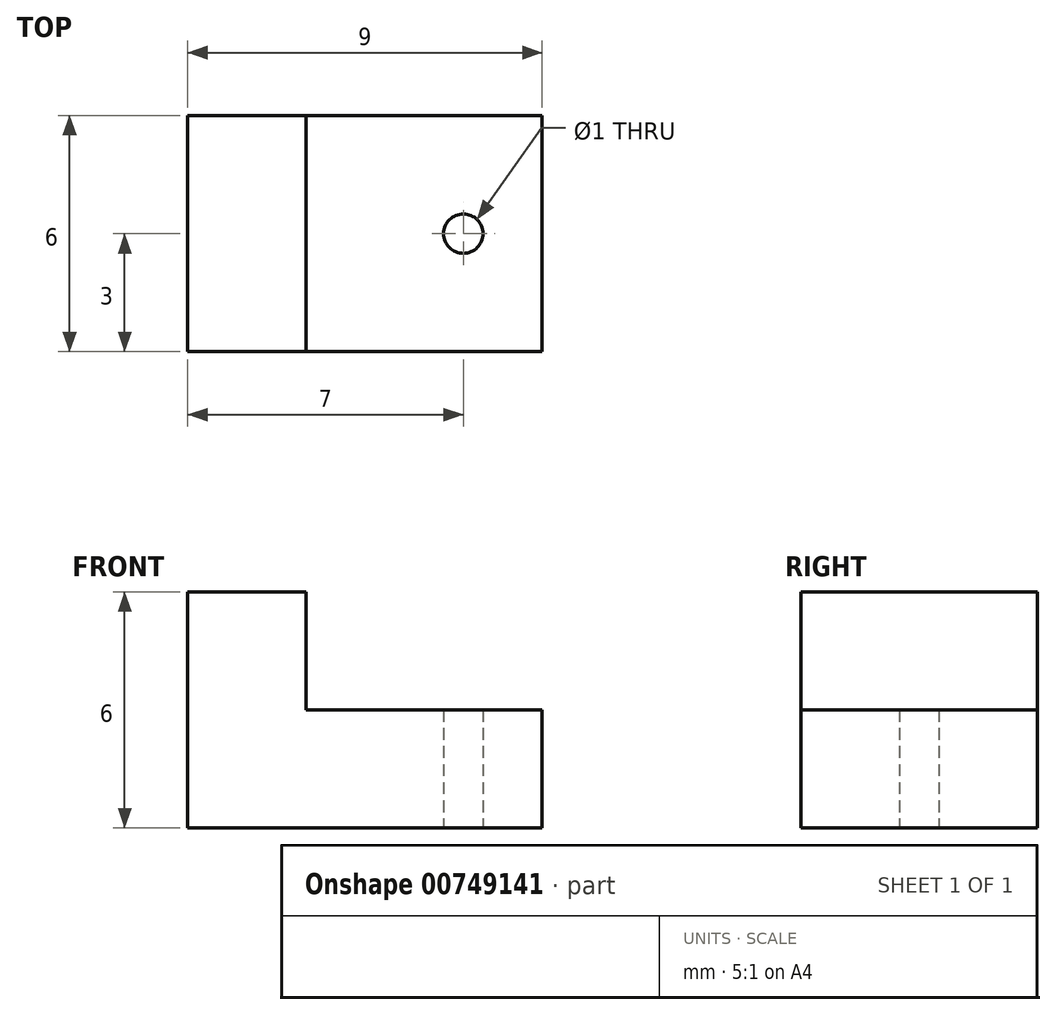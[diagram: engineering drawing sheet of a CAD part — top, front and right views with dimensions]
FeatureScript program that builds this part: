
annotation { "Feature Type Name" : "Feature", "Feature Type Description" : "" }
export const myFeature = defineFeature(function(context is Context, id is Id, definition is map)
    precondition{}
    {
        {
            var Q0;
            Q0=qCreatedBy(makeId("Top.planeOp"),FACE);
            var sketch = newSketch(context, id + "F0", { "sketchPlane" : qUnion([Q0])});
            skLineSegment(sketch, "E0.bottom", {"start": v(2, 3) * mm, "end": v(-4, 3) * mm});
            skLineSegment(sketch, "E0.top", {"start": v(2, -3) * mm, "end": v(-4, -3) * mm});
            skLineSegment(sketch, "E0.left", {"start": v(2, 3) * mm, "end": v(2, -3) * mm});
            skLineSegment(sketch, "E0.right", {"start": v(-4, 3) * mm, "end": v(-4, -3) * mm});
            skPoint(sketch, "E0.middle", {"position": v(0, 0) * mm});
            skLineSegment(sketch, "E1.bottom", {"start": v(-4, 3) * mm, "end": v(-7, 3) * mm});
            skLineSegment(sketch, "E1.top", {"start": v(-4, -3) * mm, "end": v(-7, -3) * mm});
            skLineSegment(sketch, "E1.right", {"start": v(-7, 3) * mm, "end": v(-7, -3) * mm});
            skCircle(sketch, "E2", {"center": v(0, 0) * mm, "radius": 0.5 * mm});
            skSolve(sketch);
        }
        {
            var Q0;
            Q0=makeQuery(id+"F0.imprint","IMPRINT",FACE,{"disambiguationData":[TD([[makeQuery(id+"F0.imprint","IMPRINT",EDGE,{"derivedFrom":sQuery(id+"F0.wireOp",EDGE,"E1.bottom")}),1.0]])]});
            extrude(context, id + "F1", {"entities" : qUnion([Q0]), "depth" : 6 * mm, "offsetDistance" : 25 * mm});
        }
        {
            var Q0;
            Q0=makeQuery(id+"F0.imprint","IMPRINT",FACE,{"disambiguationData":[TD([[makeQuery(id+"F0.imprint","IMPRINT",EDGE,{"derivedFrom":sQuery(id+"F0.wireOp",EDGE,"E0.bottom")}),1.0]])]});
            extrude(context, id + "F2", {"entities" : qUnion([Q0]), "operationType" : NewBodyOperationType.ADD, "depth" : 3 * mm, "offsetDistance" : 25 * mm});
        }
    });
